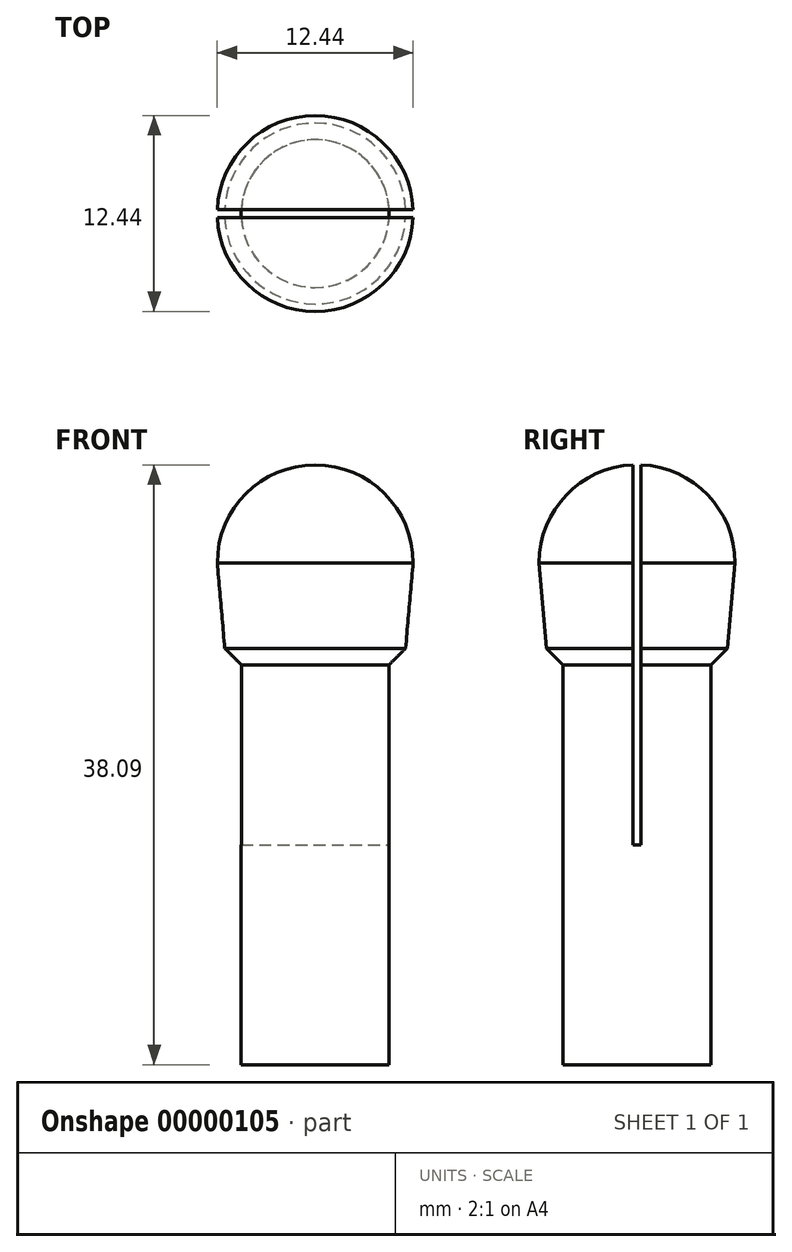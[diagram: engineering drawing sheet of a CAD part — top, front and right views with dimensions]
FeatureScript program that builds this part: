
annotation { "Feature Type Name" : "Feature", "Feature Type Description" : "" }
export const myFeature = defineFeature(function(context is Context, id is Id, definition is map)
    precondition{}
    {
        {
            var Q0;
            Q0=qCreatedBy(makeId("Front.planeOp"),FACE);
            var sketch = newSketch(context, id + "F0", { "sketchPlane" : qUnion([Q0])});
            skLineSegment(sketch, "E0", {"start": v(0, 0) * mm, "end": v(0, 38.1) * mm});
            skLineSegment(sketch, "E1", {"start": v(0, 0) * mm, "end": v(4.7, 0) * mm});
            skLineSegment(sketch, "E2", {"start": v(4.7, 0) * mm, "end": v(4.7, 25.4) * mm});
            skLineSegment(sketch, "E3", {"start": v(4.7, 25.4) * mm, "end": v(5.75, 26.45) * mm});
            skLineSegment(sketch, "E4", {"start": v(5.75, 26.45) * mm, "end": v(6.22, 31.88) * mm});
            skArc(sketch, "E5", {"start": v(6.22, 31.88) * mm, "mid": v(4.4, 36.28) * mm, "end": v(0, 38.1) * mm});
            skLineSegment(sketch, "E6", {"start": v(0, 38.1) * mm, "end": v(-10.35, 38.1) * mm, "construction": true});
            skLineSegment(sketch, "E7", {"start": v(6.22, 31.88) * mm, "end": v(6.22, 17.5) * mm, "construction": true});
            skSolve(sketch);
        }
        {
            var Q0;
            Q0=makeQuery(id+"F0.imprint","IMPRINT",FACE,{"disambiguationData":[TD([[makeQuery(id+"F0.imprint","IMPRINT",EDGE,{"derivedFrom":sQuery(id+"F0.wireOp",EDGE,"E0")}),-1.0]])]});
            var Q1;
            Q1=sQuery(id+"F0.wireOp",EDGE,"E0");
            revolve(context, id + "F1", {"entities" : qUnion([Q0]), "axis" : qUnion([Q1]), "revolveType" : RevolveType.FULL});
        }
        {
            var Q0;
            Q0=qCreatedBy(makeId("Right.planeOp"),FACE);
            var sketch = newSketch(context, id + "F2", { "sketchPlane" : qUnion([Q0])});
            skLineSegment(sketch, "E8.rect.bottom", {"start": v(0.25, 38.35) * mm, "end": v(-0.25, 38.35) * mm});
            skLineSegment(sketch, "E8.rect.top", {"start": v(0.25, 13.97) * mm, "end": v(-0.25, 13.97) * mm});
            skLineSegment(sketch, "E8.rect.left", {"start": v(0.25, 38.35) * mm, "end": v(0.25, 13.97) * mm});
            skLineSegment(sketch, "E8.rect.right", {"start": v(-0.25, 38.35) * mm, "end": v(-0.25, 13.97) * mm});
            skPoint(sketch, "E8.rect.middle", {"position": v(0, 26.16) * mm});
            skLineSegment(sketch, "E9", {"start": v(0, 26.16) * mm, "end": v(0, 0) * mm});
            skSolve(sketch);
        }
        {
            var Q0;
            Q0=makeQuery(id+"F2.imprint","IMPRINT",FACE,{"disambiguationData":[TD([[makeQuery(id+"F2.imprint","IMPRINT",EDGE,{"derivedFrom":sQuery(id+"F2.wireOp",EDGE,"E8.rect.bottom")}),1.0]])]});
            extrude(context, id + "F3", {"entities" : qUnion([Q0]), "operationType" : NewBodyOperationType.REMOVE, "endBound" : BoundingType.SYMMETRIC, "oppositeDirection" : true, "depth" : 76.2 * mm});
        }
    });
